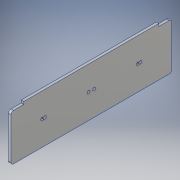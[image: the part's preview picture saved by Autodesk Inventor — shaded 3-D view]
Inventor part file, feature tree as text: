
AUTODESK INVENTOR PART (.ipt)
format: ipt  version: 2018.3 (Build 223284000, 284)  size: 135,680 bytes
history: native  units: in
note: dims shown in document units (in); Inventor stores cm internally (conversion verified against a paired STEP export)
features: other x2, sketch x1, sheet_metal_op x1
ambient origin geometry x8: Origin, YZ Plane, XZ Plane, XY Plane, X Axis, Y Axis, Z Axis, Center Point
bodies: Solid1 (feature_tree)
feature tree (4):
  sketch  "Sketch1"  dims[d0=0.125in d7=0.125in d8=0.0in]
  sheet_metal_op  "Face1"
  other  "Plate1"
  other  "Cut4"
